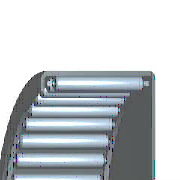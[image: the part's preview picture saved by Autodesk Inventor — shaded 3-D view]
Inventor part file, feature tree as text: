
AUTODESK INVENTOR PART (.ipt)
format: ipt  version: 2025.2 (Build 292293000, 293)  size: 282,624 bytes
history: native  units: mm (DEFAULTED — no unit token found)
features: other x3, pattern_circular x1
ambient origin geometry x8: Origin, YZ Plane, XZ Plane, XY Plane, X Axis, Y Axis, Z Axis, Center Point
bodies: Solid1 (feature_tree)
feature tree (4):
  other  "Körper"
  other  "Nut"
  other  "Rolle"
  pattern_circular  "Nuten"  Angle=90.0deg  [1 undecoded]
note: 1 required parameter value undecoded (feature->parameter linkage not recoverable at this tier; creation-order binding heuristic only, values carry confidence <= 0.55)
